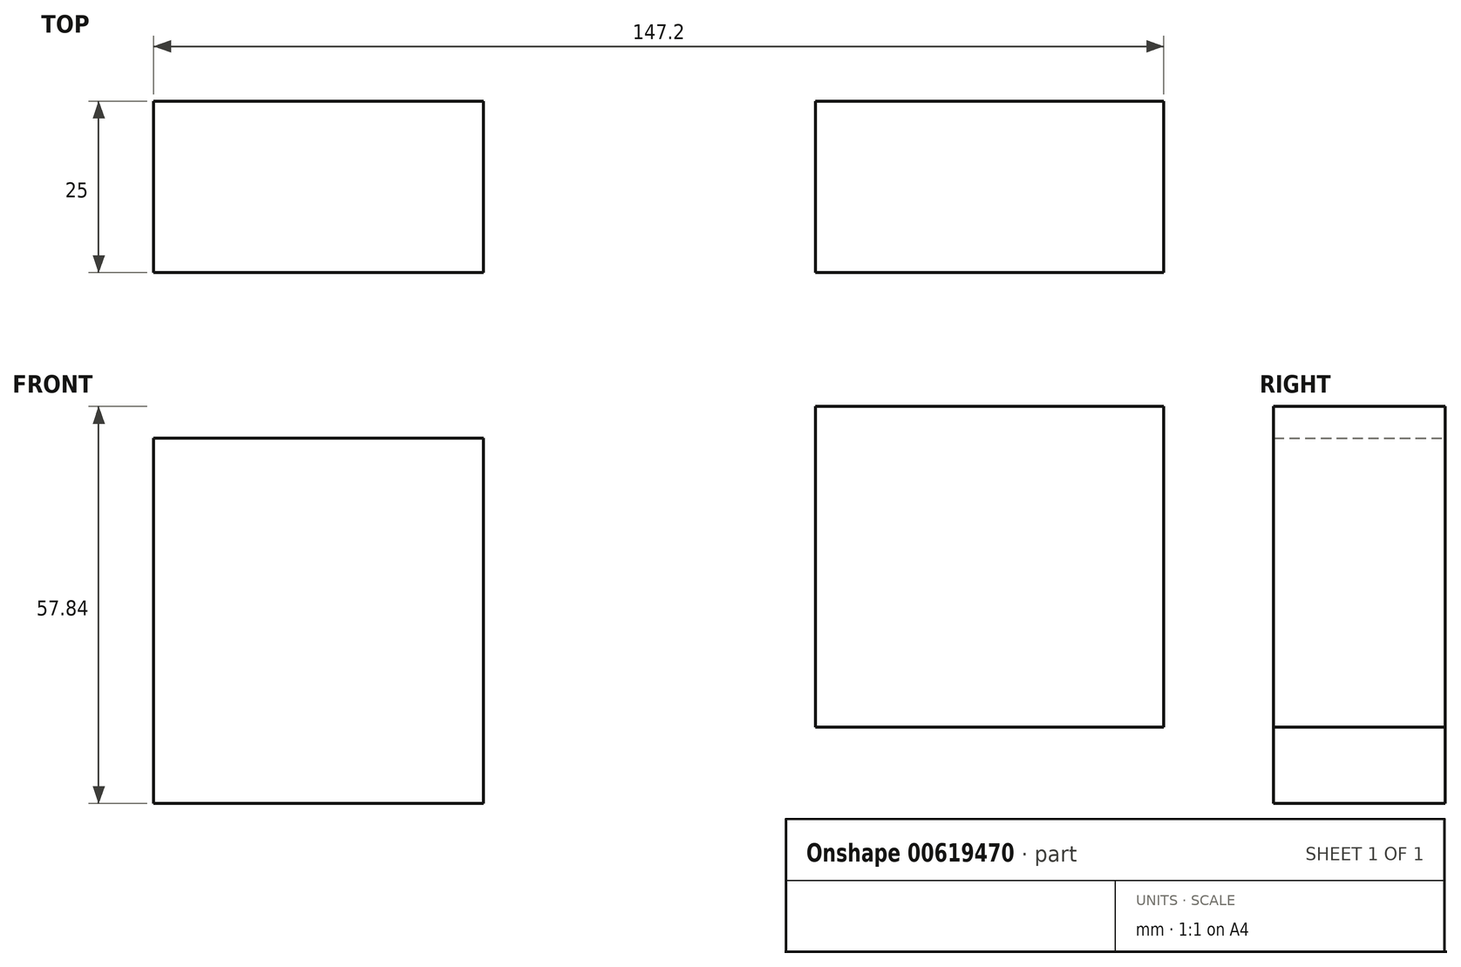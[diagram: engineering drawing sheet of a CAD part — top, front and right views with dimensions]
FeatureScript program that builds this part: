
annotation { "Feature Type Name" : "Feature", "Feature Type Description" : "" }
export const myFeature = defineFeature(function(context is Context, id is Id, definition is map)
    precondition{}
    {
        {
            var Q0;
            Q0=qCreatedBy(makeId("Front.planeOp"),FACE);
            var sketch = newSketch(context, id + "F0", { "sketchPlane" : qUnion([Q0])});
            skLineSegment(sketch, "E0.bottom", {"start": v(-93.96, 13.1) * mm, "end": v(-45.9, 13.1) * mm});
            skLineSegment(sketch, "E0.top", {"start": v(-93.96, 66.36) * mm, "end": v(-45.9, 66.36) * mm});
            skLineSegment(sketch, "E0.left", {"start": v(-93.96, 13.1) * mm, "end": v(-93.96, 66.36) * mm});
            skLineSegment(sketch, "E0.right", {"start": v(-45.9, 13.1) * mm, "end": v(-45.9, 66.36) * mm});
            skPoint(sketch, "E0.middle", {"position": v(-69.93, 39.73) * mm});
            skLineSegment(sketch, "E1.bottom", {"start": v(2.5, 24.25) * mm, "end": v(53.24, 24.25) * mm});
            skLineSegment(sketch, "E1.top", {"start": v(2.5, 70.94) * mm, "end": v(53.24, 70.94) * mm});
            skLineSegment(sketch, "E1.left", {"start": v(2.5, 24.25) * mm, "end": v(2.5, 70.94) * mm});
            skLineSegment(sketch, "E1.right", {"start": v(53.24, 24.25) * mm, "end": v(53.24, 70.94) * mm});
            skPoint(sketch, "E1.middle", {"position": v(27.87, 47.6) * mm});
            skSolve(sketch);
        }
        {
            var Q0;
            Q0=makeQuery(id+"F0.imprint","IMPRINT",FACE,{"disambiguationData":[TD([[makeQuery(id+"F0.imprint","IMPRINT",EDGE,{"derivedFrom":sQuery(id+"F0.wireOp",EDGE,"E0.bottom")}),1.0]])]});
            var Q1;
            Q1=makeQuery(id+"F0.imprint","IMPRINT",FACE,{"disambiguationData":[TD([[makeQuery(id+"F0.imprint","IMPRINT",EDGE,{"derivedFrom":sQuery(id+"F0.wireOp",EDGE,"E1.bottom")}),1.0]])]});
            extrude(context, id + "F1", {"entities" : qUnion([Q0, Q1]), "depth" : 25 * mm, "offsetDistance" : 25 * mm});
        }
    });
